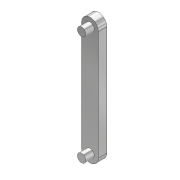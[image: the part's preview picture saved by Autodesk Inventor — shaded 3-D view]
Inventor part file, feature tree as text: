
AUTODESK INVENTOR PART (.ipt)
format: ipt  version: 2021 (Build 250183000, 183)  size: 112,128 bytes
history: native  units: mm
features: extrude x2, sketch x2, fillet x1, projected_geometry x1
ambient origin geometry x8: Origin, YZ Plane, XZ Plane, XY Plane, X Axis, Y Axis, Z Axis, Center Point
bodies: Solid1 (feature_tree)
feature tree (6):
  extrude  "Extrusion1"  Depth=20.0mm
  extrude  "Extrusion2"  Depth=10.0mm
  fillet  "Fillet1"  Radius=10.0mm
  sketch  "Sketch1"  dims[d0=130.0mm d1=20.0mm]
  sketch  "Sketch2"  dims[d2=20.0mm d3=10.0mm d4=10.0mm d5=10.0mm d6=0.0mm d7=10.0mm d8=10.0mm d9=10.0mm d10=0.0mm d11=2.0mm]
  projected_geometry  "Projected Loop1"
